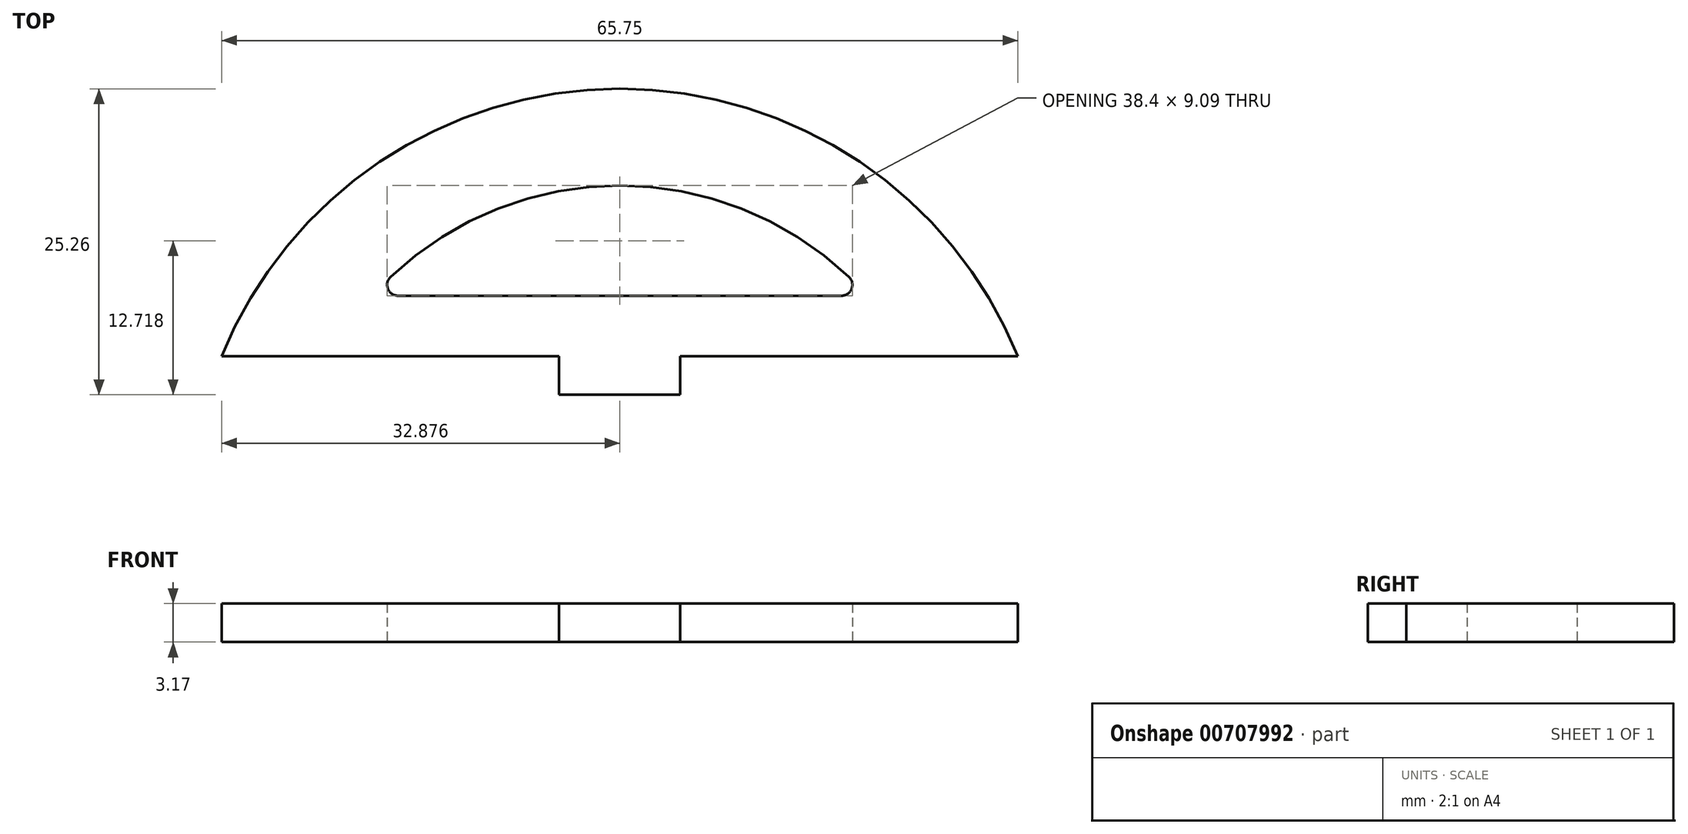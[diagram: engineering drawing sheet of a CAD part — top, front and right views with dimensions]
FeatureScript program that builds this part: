
annotation { "Feature Type Name" : "Feature", "Feature Type Description" : "" }
export const myFeature = defineFeature(function(context is Context, id is Id, definition is map)
    precondition{}
    {
        {
            var Q0;
            Q0=qCreatedBy(makeId("Top.planeOp"), FACE);
            var sketch = newSketch(context, id + "F0", { "sketchPlane" : qUnion([Q0])});
            skPoint(sketch, "E0.0", {"position": v(-31.08, 35.71) * mm});
            skArc(sketch, "E1", {"start": v(34.67, 35.71) * mm, "mid": v(1.8, 57.8) * mm, "end": v(-31.08, 35.71) * mm});
            skLineSegment(sketch, "E2", {"start": v(1.8, 32.54) * mm, "end": v(6.8, 32.54) * mm});
            skLineSegment(sketch, "E3", {"start": v(6.8, 32.54) * mm, "end": v(6.8, 35.71) * mm});
            skLineSegment(sketch, "E4.MirrorCS", {"start": v(1.8, 32.54) * mm, "end": v(-3.2, 32.54) * mm});
            skLineSegment(sketch, "E5.MirrorCS", {"start": v(-3.2, 32.54) * mm, "end": v(-3.2, 35.71) * mm});
            skLineSegment(sketch, "E6", {"start": v(-31.08, 35.71) * mm, "end": v(-3.2, 35.71) * mm});
            skLineSegment(sketch, "E7", {"start": v(6.8, 35.71) * mm, "end": v(34.67, 35.71) * mm});
            skArc(sketch, "E8.0", {"start": v(20.72, 42.26) * mm, "mid": v(1.8, 49.8) * mm, "end": v(-17.12, 42.26) * mm});
            skLineSegment(sketch, "E9", {"start": v(-16.5, 40.71) * mm, "end": v(20.1, 40.71) * mm});
            skPoint(sketch, "E10.visualSharp", {"position": v(-18.64, 40.71) * mm});
            skArc(sketch, "E10.filletArc", {"start": v(-17.12, 42.26) * mm, "mid": v(-17.34, 41.28) * mm, "end": v(-16.5, 40.71) * mm});
            skPoint(sketch, "E11.visualSharp", {"position": v(22.23, 40.71) * mm});
            skArc(sketch, "E11.filletArc", {"start": v(20.1, 40.71) * mm, "mid": v(20.93, 41.28) * mm, "end": v(20.72, 42.26) * mm});
            skSolve(sketch);
        }
        {
            var Q0;
            Q0 = qSketchRegion(id + "F0", true);
            extrude(context, id + "F1", {"entities" : qUnion([Q0]), "depth" : 3.17 * mm, "offsetDistance" : 25 * mm});
        }
    });
